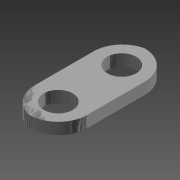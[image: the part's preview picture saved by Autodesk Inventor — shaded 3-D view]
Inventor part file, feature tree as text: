
AUTODESK INVENTOR PART (.ipt)
format: ipt  version: 2015 (Build 190159000, 159)  size: 106,496 bytes
history: native  units: mm
features: other x3, sketch x2, hole x1, fillet x1
ambient origin geometry x8: Origin, YZ Plane, XZ Plane, XY Plane, X Axis, Y Axis, Z Axis, Center Point
bodies: Body1 (feature_tree)
feature tree (7):
  other  "Bryła1"
  other  "Powierzchnia1"
  hole  "Otwór1"  [1 undecoded]
  fillet  "Zaokrąglenie1"  Radius=9.0mm
  sketch  "Szkic1"
  other  "Płyta1"
  sketch  "Szkic2"
note: 1 required parameter value undecoded (feature->parameter linkage not recoverable at this tier; creation-order binding heuristic only, values carry confidence <= 0.55)
